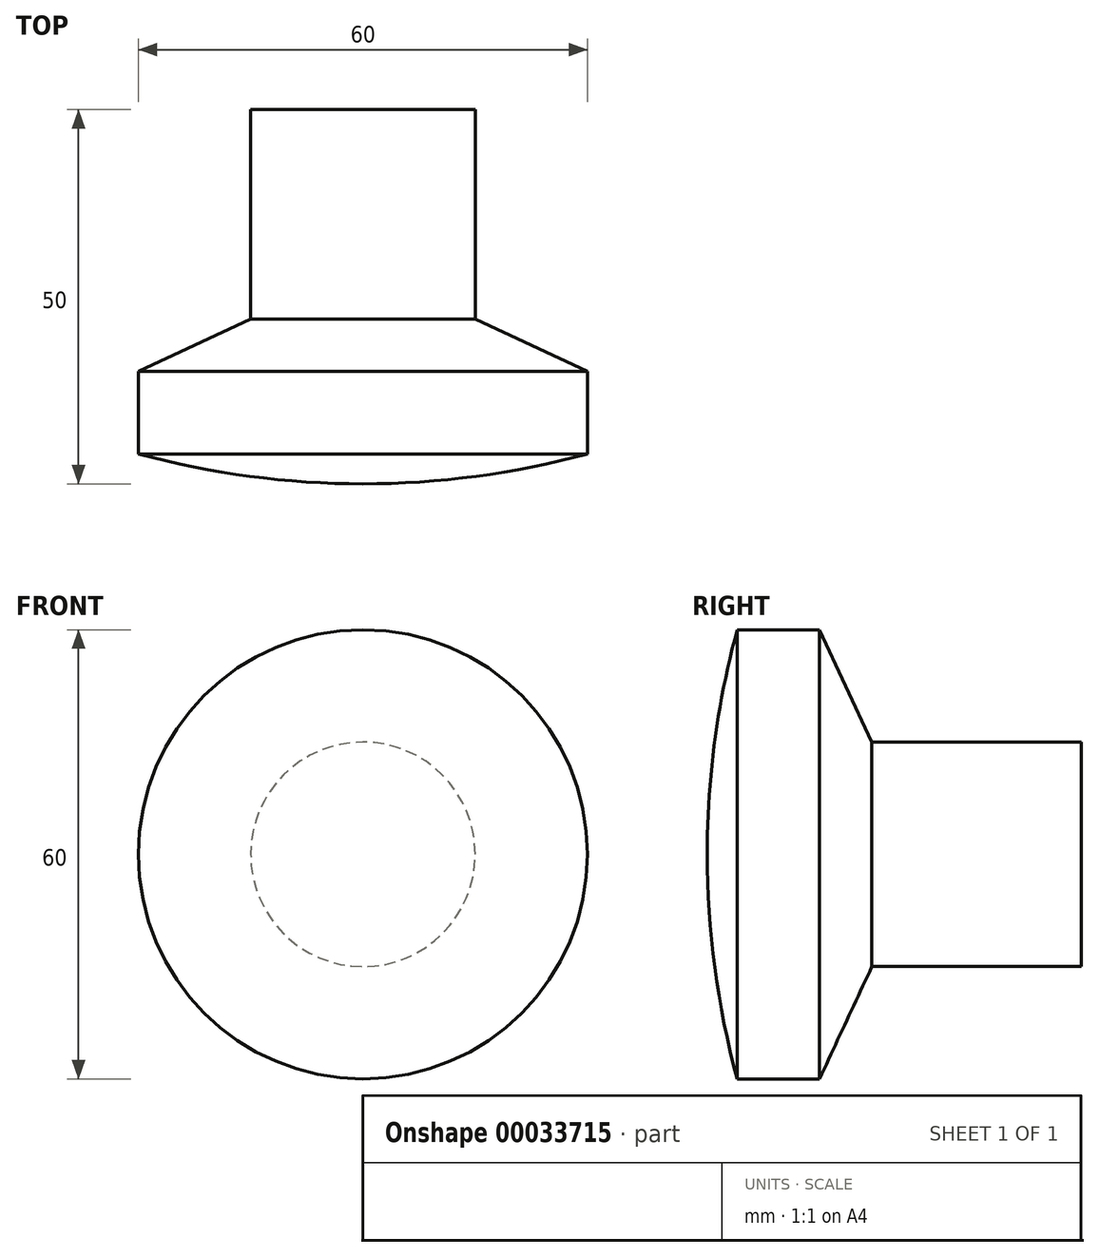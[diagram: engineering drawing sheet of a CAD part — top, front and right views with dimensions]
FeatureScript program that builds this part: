
annotation { "Feature Type Name" : "Feature", "Feature Type Description" : "" }
export const myFeature = defineFeature(function(context is Context, id is Id, definition is map)
    precondition{}
    {
        {
            var Q0;
            Q0=qCreatedBy(makeId("Front.planeOp"),FACE);
            var sketch = newSketch(context, id + "F0", { "sketchPlane" : qUnion([Q0])});
            skCircle(sketch, "E0", {"center": v(0, 0) * mm, "radius": 15 * mm});
            skSolve(sketch);
        }
        {
            var Q0;
            Q0=makeQuery(id+"F0.imprint","IMPRINT",FACE,{"disambiguationData":[TD([[makeQuery(id+"F0.imprint","IMPRINT",EDGE,{"derivedFrom":sQuery(id+"F0.wireOp",EDGE,"E0")}),1.0]])]});
            extrude(context, id + "F1", {"entities" : qUnion([Q0]), "depth" : 28 * mm});
        }
        {
            var Q0;
            Q0=qCreatedBy(makeId("Right.planeOp"),FACE);
            var sketch = newSketch(context, id + "F2", { "sketchPlane" : qUnion([Q0])});
            skPoint(sketch, "E1", {"position": v(-35, 30) * mm});
            skPoint(sketch, "E2", {"position": v(-32.58, -21.35) * mm});
            skPoint(sketch, "E3", {"position": v(-32.89, -22.99) * mm});
            skLineSegment(sketch, "E4.0", {"start": v(-28, -15) * mm, "end": v(-28, 15) * mm});
            skLineSegment(sketch, "E5", {"start": v(-28, 15) * mm, "end": v(0, 15) * mm});
            skLineSegment(sketch, "E6", {"start": v(-28, 15) * mm, "end": v(-35, 30) * mm});
            skLineSegment(sketch, "E7", {"start": v(-35, 30) * mm, "end": v(-35, 0) * mm});
            skLineSegment(sketch, "E8", {"start": v(-35, 0) * mm, "end": v(-28, 0) * mm});
            skLineSegment(sketch, "E9", {"start": v(-28, 0) * mm, "end": v(-28, 15) * mm});
            skSolve(sketch);
        }
        {
            var Q0;
            Q0=makeQuery(id+"F2.imprint","IMPRINT",FACE,{"disambiguationData":[TD([[makeQuery(id+"F2.imprint","IMPRINT",EDGE,{"derivedFrom":sQuery(id+"F2.wireOp",EDGE,"E6")}),1.0]])]});
            var Q1;
            Q1=sQuery(id+"F2.wireOp",EDGE,"E8");
            revolve(context, id + "F3", {"operationType" : NewBodyOperationType.ADD, "entities" : qUnion([Q0]), "axis" : qUnion([Q1]), "revolveType" : RevolveType.FULL});
        }
        {
            var Q0;
            Q0=makeQuery(id+"F3.opRevolve","SWEPT_FACE",FACE,{"disambiguationData":[OSD([sQuery(id+"F2.wireOp",EDGE,"E7")])]});
            var sketch = newSketch(context, id + "F4", { "sketchPlane" : qUnion([Q0])});
            skSolve(sketch);
        }
        {
            var Q0;
            Q0=makeQuery(id+"F4.imprint","IMPRINT",FACE,{"disambiguationData":[TD([[makeQuery(id+"F4.imprint","IMPRINT",EDGE,{"derivedFrom":makeQuery(id+"F3.opRevolve","SWEPT_EDGE",EDGE,{"disambiguationData":[OSD([sQuery(id+"F2.wireOp",EDGE,"E6"),sQuery(id+"F2.wireOp",EDGE,"E7")])]})}),1.0]])]});
            extrude(context, id + "F5", {"entities" : qUnion([Q0]), "operationType" : NewBodyOperationType.ADD, "depth" : 11 * mm});
        }
        {
            var Q0;
            Q0=qCreatedBy(makeId("Right.planeOp"),FACE);
            var sketch = newSketch(context, id + "F6", { "sketchPlane" : qUnion([Q0])});
            skLineSegment(sketch, "E10.0", {"start": v(-46, -30) * mm, "end": v(-46, 30) * mm});
            skArc(sketch, "E11", {"start": v(-46, 30) * mm, "mid": v(-49, 15.13) * mm, "end": v(-50, 0) * mm});
            skLineSegment(sketch, "E12", {"start": v(-50, 0) * mm, "end": v(-46, 0) * mm});
            skLineSegment(sketch, "E13", {"start": v(-46, 30) * mm, "end": v(-46, 0) * mm});
            skSolve(sketch);
        }
        {
            var Q0;
            Q0=makeQuery(id+"F6.imprint","IMPRINT",FACE,{"disambiguationData":[TD([[makeQuery(id+"F6.imprint","IMPRINT",EDGE,{"derivedFrom":sQuery(id+"F6.wireOp",EDGE,"E11")}),1.0]])]});
            var Q1;
            Q1=sQuery(id+"F6.wireOp",EDGE,"E12");
            revolve(context, id + "F7", {"operationType" : NewBodyOperationType.ADD, "entities" : qUnion([Q0]), "axis" : qUnion([Q1]), "revolveType" : RevolveType.FULL});
        }
    });
